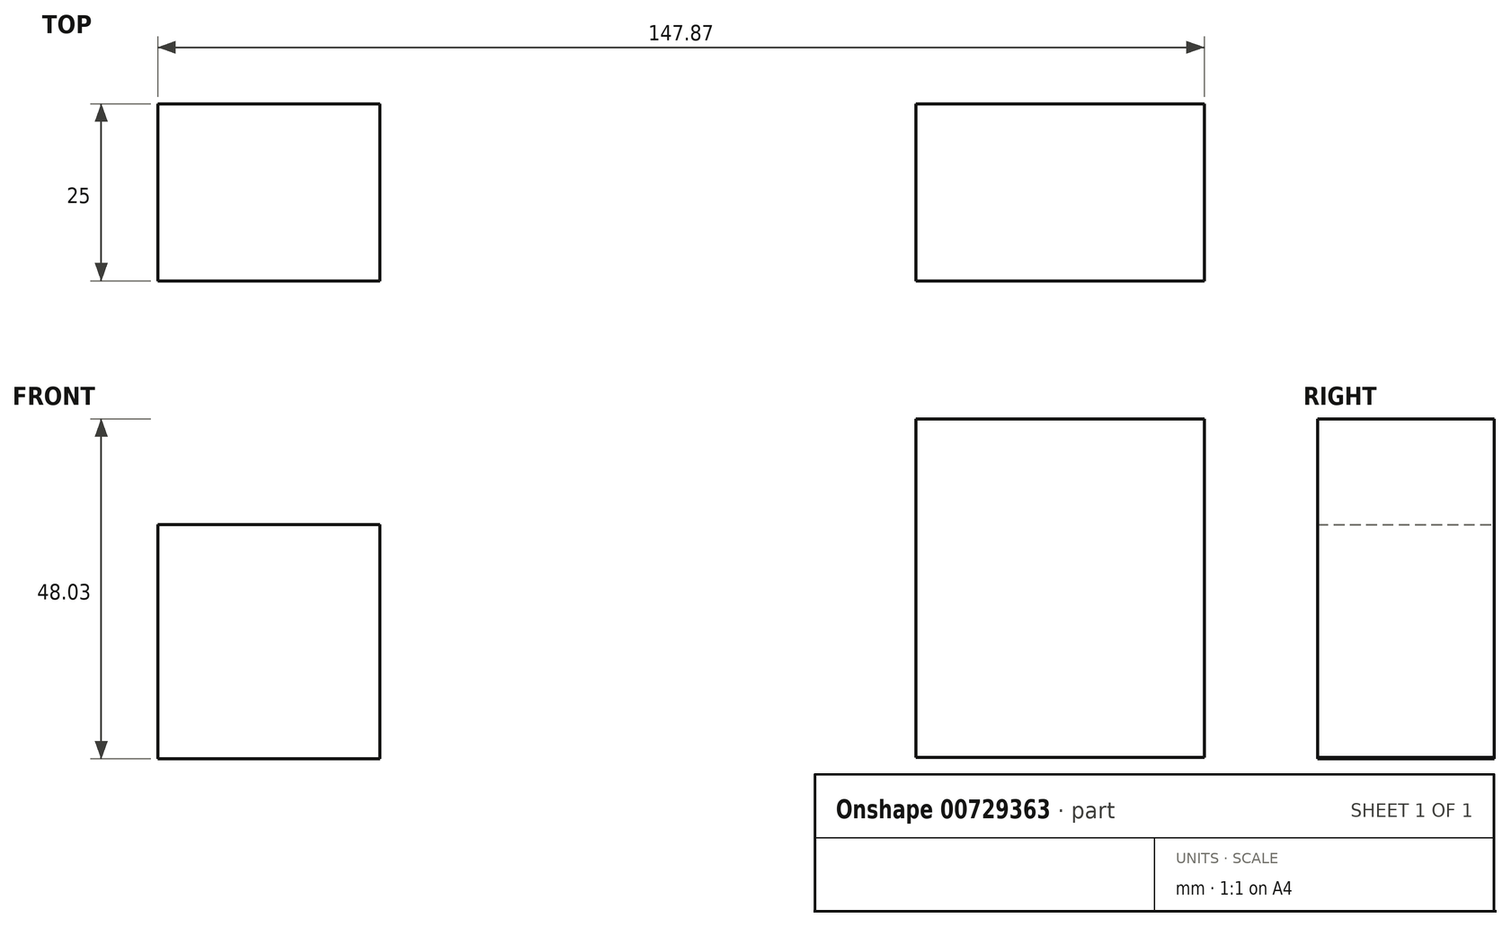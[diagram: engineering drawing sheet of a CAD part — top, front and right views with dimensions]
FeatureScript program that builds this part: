
annotation { "Feature Type Name" : "Feature", "Feature Type Description" : "" }
export const myFeature = defineFeature(function(context is Context, id is Id, definition is map)
    precondition{}
    {
        {
            var Q0;
            Q0=qCreatedBy(makeId("Front.planeOp"),FACE);
            var sketch = newSketch(context, id + "F0", { "sketchPlane" : qUnion([Q0])});
            skLineSegment(sketch, "E0.bottom", {"start": v(-139.69, -11.12) * mm, "end": v(-108.31, -11.12) * mm});
            skLineSegment(sketch, "E0.top", {"start": v(-139.69, 21.97) * mm, "end": v(-108.31, 21.97) * mm});
            skLineSegment(sketch, "E0.left", {"start": v(-139.69, -11.12) * mm, "end": v(-139.69, 21.97) * mm});
            skLineSegment(sketch, "E0.right", {"start": v(-108.31, -11.12) * mm, "end": v(-108.31, 21.97) * mm});
            skPoint(sketch, "E0.middle", {"position": v(-124, 5.43) * mm});
            skLineSegment(sketch, "E1.bottom", {"start": v(-32.54, -10.9) * mm, "end": v(8.18, -10.9) * mm});
            skLineSegment(sketch, "E1.top", {"start": v(-32.54, 36.9) * mm, "end": v(8.18, 36.9) * mm});
            skLineSegment(sketch, "E1.left", {"start": v(-32.54, -10.9) * mm, "end": v(-32.54, 36.9) * mm});
            skLineSegment(sketch, "E1.right", {"start": v(8.18, -10.9) * mm, "end": v(8.18, 36.9) * mm});
            skPoint(sketch, "E1.middle", {"position": v(-12.18, 13) * mm});
            skSolve(sketch);
        }
        {
            var Q0;
            Q0=makeQuery(id+"F0.imprint","IMPRINT",FACE,{"disambiguationData":[TD([[makeQuery(id+"F0.imprint","IMPRINT",EDGE,{"derivedFrom":sQuery(id+"F0.wireOp",EDGE,"E0.bottom")}),1.0]])]});
            var Q1;
            Q1=makeQuery(id+"F0.imprint","IMPRINT",FACE,{"disambiguationData":[TD([[makeQuery(id+"F0.imprint","IMPRINT",EDGE,{"derivedFrom":sQuery(id+"F0.wireOp",EDGE,"E1.bottom")}),1.0]])]});
            extrude(context, id + "F1", {"entities" : qUnion([Q0, Q1]), "depth" : 25 * mm, "offsetDistance" : 25 * mm});
        }
    });
